# Revit family: Electronics_Commercial-Loudspeakers_Two-Way-Marine-Speaker_CMAR8T-W
name_source: partatom
category: Communication Devices
units: mm (PartAtom-declared; Revit-internal decimal feet)

## family parameters
Cut with Voids When Loaded = No
Host = Face
Maintain Annotation Orientation = No
OmniClass Number = 23.85.10.11.14.14.14
OmniClass Title = Loudspeakers
Part Type = Normal
Room Calculation Point = No
Round Connector Dimension = Use Diameter
Shared = No

## types (1)
- CMAR8T-W
    100V transformer power taps in watts = 20 - 10 - 5 - 2.5
    Applicable in 100V = Yes
    Applicable low impedance = Yes
    Closest RAL colour (subject to deviations) = RAL9003
    Colour = White
    Connector Description = Terminal strip; Low impedance 8 ohms/100W, 100V operation
    Cutout in mm = 151
    Default Elevation = 4' - 0"
    Depth = 0' - 3"
    Description = CMAR8T-W 8 Two-Way Built-in Marine Speaker 8 ohms/100W; 100V/20W
    Diameter = 0' - 8 1/2"
    Frequency response in Hz = 55 - 20K
    Grill Material = Biamp - Plastic - White(Grid)
    Grille main material = Stainless steel
    Housing Material = Biamp - Plastic - White
    IP rating = 65
    Impedance in ohms = 8
    Installation grip range in mm = 1 - up
    Loudspeaker system = 2-way
    Low impedance RMS power in watts = 50
    Low impedance dynamic power in watts = 100
    Main construction material = ABS plastic
    Manufacturer = Biamp
    Max SPL 1m in dB = 107
    Model = CMAR8T-W
    Mounting system = 4 screws
    Product Documentation Link = https://downloads.biamp.com
    Product Page URL = https://www.biamp.com
    Product data url = https://bimobject.com
    SPL 1W/1m in dB = 88
    Tweeter size in inch = 1
    URL = https://www.biamp.com
    Vertical dispersion angle 1000 Hz = 180°
    Weight = 3.31 lb
    Woofer cone material = Polypropylene
    Woofer size in inch = 8

## geometry (parser evidence)
native form markers: Sweep x2
no freeform markers — native parametric forms only
